# Revit family: ACRU-B
name_source: partatom
category: Mechanical Equipment
units: mm (PartAtom-declared; Revit-internal decimal feet)

## family parameters
Always vertical = Yes
Cut with Voids When Loaded = No
Part Type = Normal
Room Calculation Point = No
Round Connector Dimension = Use Diameter
Shared = No
Work Plane-Based = No

## types (38) — shared parameters
1.5" = 0' - 1 1/2"
2" = 0' - 2"
EDGE_TO_CURB = 0' - 2 1/4"
ONE EIGTH = 0' - 0 1/8"
Type Comments = Upblast Centrifugal Exhaust Ventilator Roof Mounted/Belt Drive
URL = www.lorencook.com
ZERO = 0' - 0"

## per-type parameters (varying)
| type | APLUSG | A_SUB | B_SUB | C_SUB | DEPTH | EIGHTH_T_SQ | HALF_B_SUB | INLET_HEIGHT | Manufacturer | Model | RO/2 | ROOF_OPENING | T_SQ | T_SQ_HALF | WB_RADIUS |
| 100_ACRU-B | 0' - 4 7/8" | 1' - 0 1/2" | 2' - 1 1/4" | 1' - 8 3/16" | 0' - 2" | 0' - 1 13/16" | 1' - 0 5/8" | 0' - 2 7/8" | Loren Cook Company | ACRUB | 0' - 6 3/4" | 1' - 1 1/2" | 1' - 6" | 0' - 9" | 0' - 4" |
| 120_ACRU-B | 0' - 3 13/16" | 1' - 7 1/16" | 2' - 6 3/16" | 2' - 4 1/4" | 0' - 2" | 0' - 2" | 1' - 3 3/32" | 0' - 1 13/16" | Loren Cook Company | ACRUB | 0' - 7 3/4" | 1' - 3 1/2" | 1' - 8" | 0' - 10" | 0' - 6" |
| 135_ACRU-B | 0' - 4 3/16" | 1' - 7 1/16" | 2' - 6 3/16" | 2' - 4 5/8" | 0' - 2" | 0' - 2" | 1' - 3 3/32" | 0' - 2 3/16" | Loren Cook Company | ACRUB | 0' - 7 3/4" | 1' - 3 1/2" | 1' - 8" | 0' - 10" | 0' - 6" |
| 150_ACRU-B | 0' - 5 1/16" | 1' - 8 15/16" | 2' - 10 11/16" | 2' - 6 1/4" | 0' - 2" | 0' - 2 13/32" | 1' - 5 11/32" | 0' - 3 1/16" | Loren Cook Company | ACRUB | 0' - 9 3/4" | 1' - 7 1/2" | 2' - 0" | 1' - 0" | 0' - 6" |
| 165_ACRU-B | 0' - 5 9/16" | 1' - 8 15/16" | 2' - 10 11/16" | 2' - 6 3/4" | 0' - 2" | 0' - 2 13/32" | 1' - 5 11/32" | 0' - 3 9/16" | Loren Cook Company | ACRUB | 0' - 9 3/4" | 1' - 7 1/2" | 2' - 0" | 1' - 0" | 0' - 6" |
| 180_ACRU-B | 0' - 6 15/16" | 2' - 0 13/16" | 3' - 3 7/16" | 2' - 11 7/8" | 0' - 3" | 0' - 3" | 1' - 7 23/32" | 0' - 3 15/16" | Loren Cook Company | ACRUB
ACRUB | 1' - 0 3/4" | 2' - 1 1/2" | 2' - 6" | 1' - 3" | 0' - 6" |
| 195_ACRU-B | 0' - 7 7/16" | 2' - 0 13/16" | 3' - 3 7/16" | 3' - 0 3/8" | 0' - 3" | 0' - 3" | 1' - 7 23/32" | 0' - 4 7/16" | Loren Cook Company | ACRUB | 1' - 0 3/4" | 2' - 1 1/2" | 2' - 6" | 1' - 3" | 0' - 7" |
| 210_ACRU-B | 0' - 7 3/4" | 2' - 1 15/16" | 3' - 9 1/4" | 3' - 2 3/8" | 0' - 3" | 0' - 3" | 1' - 10 5/8" | 0' - 4 3/4" | Loren Cook Company | ACRUB | 1' - 0 3/4" | 2' - 1 1/2" | 2' - 6" | 1' - 3" | 0' - 8" |
| 225_ACRU-B | 0' - 7 7/8" | 2' - 1 15/16" | 3' - 9 1/4" | 3' - 2 1/8" | 0' - 3" | 0' - 3" | 1' - 10 5/8" | 0' - 4 7/8" | Loren Cook Company
Loren Cook Company | ACRUB | 1' - 0 3/4" | 2' - 1 1/2" | 2' - 6" | 1' - 3" | 0' - 9" |
| 245_ACRU-B | 0' - 9 1/8" | 2' - 4 1/2" | 4' - 1 1/4" | 3' - 5 1/16" | 0' - 3" | 0' - 3" | 2' - 0 5/8" | 0' - 6 1/8" | Loren Cook Company | ACRUB | 1' - 0 3/4" | 2' - 1 1/2" | 2' - 6" | 1' - 3" | 0' - 9" |
| 270_ACRU-B | 0' - 9 1/8" | 2' - 4 1/2" | 4' - 1 1/4" | 3' - 5 1/16" | 0' - 3" | 0' - 3 19/32" | 2' - 0 5/8" | 0' - 6 1/8" | Loren Cook Company | ACRUB | 1' - 3 3/4" | 2' - 7 1/2" | 3' - 0" | 1' - 6" | 0' - 9" |
| 300_ACRU-B | 0' - 10 1/16" | 2' - 9 7/8" | 4' - 6 1/4" | 4' - 1 15/16" | 0' - 3" | 0' - 3 19/32" | 2' - 3 1/8" | 0' - 7 1/16" | Loren Cook Company | ACRUB | 1' - 3 3/4" | 2' - 7 1/2" | 3' - 0" | 1' - 6" | 0' - 10" |
| 330_ACRU-B | 0' - 10 5/16" | 2' - 10 1/8" | 4' - 6 1/4" | 4' - 2 7/16" | 0' - 3" | 0' - 4 3/16" | 2' - 3 1/8" | 0' - 7 5/16" | Loren Cook Company | ACRUB | 1' - 6 3/4" | 3' - 1 1/2" | 3' - 6" | 1' - 9" | 0' - 10" |
| 365_ACRU-B | 0' - 11 1/16" | 3' - 0 3/8" | 5' - 4 1/4" | 4' - 4 7/16" | 0' - 3" | 0' - 4 3/16" | 2' - 8 1/8" | 0' - 8 1/16" | Loren Cook Company | ACRUB | 1' - 6 3/4" | 3' - 1 1/2" | 3' - 6" | 1' - 9" | 1' - 0" |
| 402_ACRU-B | 1' - 1 1/16" | 3' - 1 7/8" | 5' - 4 1/4" | 4' - 6 11/16" | 0' - 3" | 0' - 4 13/16" | 2' - 8 1/8" | 0' - 10 1/16" | Loren Cook Company | ACRUB | 1' - 9 3/4" | 3' - 7 1/2" | 4' - 0" | 2' - 0" | 1' - 0" |
| 445_ACRU-B | 1' - 0 3/4" | 3' - 6 7/8" | 6' - 4 1/4" | 4' - 9 3/16" | 0' - 3" | 0' - 5 13/32" | 3' - 2 1/8" | 0' - 9 3/4" | Loren Cook Company | ACRUB | 2' - 0 3/4" | 4' - 1 1/2" | 4' - 6" | 2' - 3" | 1' - 0" |
| 490_ACRU-B | 1' - 2 1/2" | 3' - 8 5/8" | 6' - 4 1/4" | 4' - 10 1/16" | 0' - 3" | 0' - 5 13/32" | 3' - 2 1/8" | 0' - 11 1/2" | Loren Cook Company | ACRUB | 2' - 0 3/4" | 4' - 1 1/2" | 4' - 6" | 2' - 3" | 1' - 0" |
| 150_ACRU-HP | 0' - 5 1/16" | 1' - 8 15/16" | 2' - 10 11/16" | 2' - 3 1/2" | 0' - 2" | 0' - 2 13/32" | 1' - 5 11/32" | 0' - 3 1/16" | Loren Cook Company | ACRU-HP | 0' - 9 3/4" | 1' - 7 1/2" | 2' - 0" | 1' - 0" | 0' - 6" |
| 165_ACRU-HP | 0' - 5 9/16" | 1' - 8 15/16" | 2' - 10 11/16" | 2' - 3 3/4" | 0' - 2" | 0' - 2 13/32" | 1' - 5 11/32" | 0' - 3 9/16" | Loren Cook Company | ACRU-HP | 0' - 9 3/4" | 1' - 7 1/2" | 2' - 0" | 1' - 0" | 0' - 6" |
| 180_ACRU-HP | 0' - 6 15/16" | 2' - 0 13/16" | 3' - 3 7/16" | 2' - 9 3/8" | 0' - 3" | 0' - 3" | 1' - 7 23/32" | 0' - 3 15/16" | Loren Cook Company | ACRU-HP | 1' - 0 3/4" | 2' - 1 1/2" | 2' - 6" | 1' - 3" | 0' - 6" |
| 195_ACRU-HP | 0' - 7 7/16" | 2' - 0 13/16" | 3' - 3 7/16" | 2' - 9 1/2" | 0' - 3" | 0' - 3" | 1' - 7 23/32" | 0' - 4 7/16" | Loren Cook Company | ACRU-HP | 1' - 0 3/4" | 2' - 1 1/2" | 2' - 6" | 1' - 3" | 0' - 7" |
| 210_ACRU-HP | 0' - 7 3/4" | 2' - 1 15/16" | 3' - 9 1/4" | 2' - 11 3/8" | 0' - 3" | 0' - 3" | 1' - 10 5/8" | 0' - 4 3/4" | Loren Cook Company | ACRU-HP | 1' - 0 3/4" | 2' - 1 1/2" | 2' - 6" | 1' - 3" | 0' - 8" |
| 225_ACRU-HP | 0' - 7 7/8" | 2' - 1 15/16" | 3' - 9 1/4" | 2' - 11 1/2" | 0' - 3" | 0' - 3" | 1' - 10 5/8" | 0' - 4 7/8" | Loren Cook Company
Loren Cook Company | ACRU-HP | 1' - 0 3/4" | 2' - 1 1/2" | 2' - 6" | 1' - 3" | 0' - 9" |
| 245_ACRU-HP | 0' - 9 1/8" | 2' - 4 1/2" | 4' - 1 1/4" | 3' - 1 5/16" | 0' - 3" | 0' - 3" | 2' - 0 5/8" | 0' - 6 1/8" | Loren Cook Company | ACRU-HP | 1' - 0 3/4" | 2' - 1 1/2" | 2' - 6" | 1' - 3" | 0' - 9" |
| 270_ACRU-HP | 0' - 9 1/8" | 2' - 4 1/2" | 4' - 1 1/4" | 37' - 3 3/4" | 0' - 3" | 0' - 3 19/32" | 2' - 0 5/8" | 0' - 6 1/8" | Loren Cook Company | ACRU-HP | 1' - 3 3/4" | 2' - 7 1/2" | 3' - 0" | 1' - 6" | 0' - 9" |
| 300_ACRU-HP | 0' - 10 1/16" | 2' - 9 7/8" | 4' - 6 1/4" | 3' - 9 15/16" | 0' - 3" | 0' - 3 19/32" | 2' - 3 1/8" | 0' - 7 1/16" | Loren Cook Company | ACRU-HP | 1' - 3 3/4" | 2' - 7 1/2" | 3' - 0" | 1' - 6" | 0' - 10" |
| 330_ACRU-HP | 0' - 10 5/16" | 2' - 10 1/8" | 4' - 6 1/4" | 3' - 10 11/16" | 0' - 3" | 0' - 4 3/16" | 2' - 3 1/8" | 0' - 7 5/16" | Loren Cook Company | ACRU-HP | 1' - 6 3/4" | 3' - 1 1/2" | 3' - 6" | 1' - 9" | 0' - 10" |
| 365_ACRU-HP | 0' - 11 1/16" | 3' - 0 3/8" | 5' - 4 1/4" | 4' - 0 7/16" | 0' - 3" | 0' - 4 3/16" | 2' - 8 1/8" | 0' - 8 1/16" | Loren Cook Company | ACRU-HP | 1' - 6 3/4" | 3' - 1 1/2" | 3' - 6" | 1' - 9" | 1' - 0" |
| 165_ACRU-XP | 0' - 5 9/16" | 1' - 8 15/16" | 2' - 10 11/16" | 2' - 2 11/16" | 0' - 2" | 0' - 2 13/32" | 1' - 5 11/32" | 0' - 3 9/16" | Loren Cook Company | ACRU-XP | 0' - 9 3/4" | 1' - 7 1/2" | 2' - 0" | 1' - 0" | 0' - 6" |
| 180_ACRU-XP | 0' - 6 15/16" | 2' - 0 13/16" | 3' - 3 7/16" | 2' - 7 9/16" | 0' - 3" | 0' - 3" | 1' - 7 23/32" | 0' - 3 15/16" | Loren Cook Company | ACRU-XP | 1' - 0 3/4" | 2' - 1 1/2" | 2' - 6" | 1' - 3" | 0' - 6" |
| 195_ACRU-XP | 0' - 7 7/16" | 2' - 0 13/16" | 3' - 3 7/16" | 2' - 8 1/8" | 0' - 3" | 0' - 3" | 1' - 7 23/32" | 0' - 4 7/16" | Loren Cook Company | ACRU-XP | 1' - 0 3/4" | 2' - 1 1/2" | 2' - 6" | 1' - 3" | 0' - 7" |
| 210_ACRU-XP | 0' - 7 3/4" | 2' - 1 15/16" | 3' - 9 1/4" | 2' - 8 3/4" | 0' - 3" | 0' - 3" | 1' - 10 5/8" | 0' - 4 3/4" | Loren Cook Company | ACRU-XP | 1' - 0 3/4" | 2' - 1 1/2" | 2' - 6" | 1' - 3" | 0' - 8" |
| 225_ACRU-XP | 0' - 7 7/8" | 2' - 1 15/16" | 3' - 9 1/4" | 2' - 9 5/16" | 0' - 3" | 0' - 3" | 1' - 10 5/8" | 0' - 4 7/8" | Loren Cook Company
Loren Cook Company | ACRU-XP | 1' - 0 3/4" | 2' - 1 1/2" | 2' - 6" | 1' - 3" | 0' - 9" |
| 245_ACRU-XP | 0' - 9 1/8" | 2' - 4 1/2" | 4' - 1 1/4" | 34' - 0 3/4" | 0' - 3" | 0' - 3" | 2' - 0 5/8" | 0' - 6 1/8" | Loren Cook Company | ACRU-XP | 1' - 0 3/4" | 2' - 1 1/2" | 2' - 6" | 1' - 3" | 0' - 9" |
| 270_ACRU-XP | 0' - 9 1/8" | 2' - 4 1/2" | 4' - 1 1/4" | 35' - 0" | 0' - 3" | 0' - 3 19/32" | 2' - 0 5/8" | 0' - 6 1/8" | Loren Cook Company | ACRU-XP | 1' - 3 3/4" | 2' - 7 1/2" | 3' - 0" | 1' - 6" | 0' - 9" |
| 300_ACRU-XP | 0' - 10 1/16" | 2' - 9 7/8" | 4' - 6 1/4" | 3' - 5 7/16" | 0' - 3" | 0' - 3 19/32" | 2' - 3 1/8" | 0' - 7 1/16" | Loren Cook Company | ACRU-XP | 1' - 3 3/4" | 2' - 7 1/2" | 3' - 0" | 1' - 6" | 0' - 10" |
| 330_ACRU-XP | 0' - 10 5/16" | 2' - 10 1/8" | 4' - 6 1/4" | 3' - 7 1/8" | 0' - 3" | 0' - 4 3/16" | 2' - 3 1/8" | 0' - 7 5/16" | Loren Cook Company | ACRU-XP | 1' - 6 3/4" | 3' - 1 1/2" | 3' - 6" | 1' - 9" | 0' - 10" |
| 365_ACRU-XP | 0' - 11 1/16" | 3' - 0 3/8" | 5' - 4 1/4" | 3' - 8 1/4" | 0' - 3" | 0' - 4 3/16" | 2' - 8 1/8" | 0' - 8 1/16" | Loren Cook Company | ACRU-XP | 1' - 6 3/4" | 3' - 1 1/2" | 3' - 6" | 1' - 9" | 1' - 0" |

## geometry (parser evidence)
native form markers: Sweep x1
no freeform markers — native parametric forms only
